# Revit family: ATI - Variable Frequency AC Drive
name_source: partatom
category: Electrical Equipment
revit_build: Autodesk Revit 2014 (Build: 20131024_2115(x64)
units: mm (PartAtom-declared; Revit-internal decimal feet)

## types (4) — shared parameters
Apparent Load A = 0 VA
Apparent Load B = 0 VA
Apparent Load C = 0 VA
Cabinet Material = <By Category>
Circuit Breaker Disconnect Material = <By Category>
Default Elevation = 4' - 0"
Drive Controller Voltage = 460 V
Drive Width = 1' - 1 3/4"
Load Classification = Other
Number of Poles = 3
Pilot Light Material = <By Category>
Pushbotton Material = <By Category>

## per-type parameters (varying)
| type | Drive Height | Drive Length | Front Clearance Depth | Half Drive Length |
| 1-7.5 HP | 3' - 2" | 1' - 7 1/2" | 3' - 0" | 0' - 9 3/4" |
| 10-20 HP | 3' - 2" | 1' - 7 1/2" | 3' - 0" | 0' - 9 3/4" |
| 25-50 HP | 3' - 10" | 1' - 8" | 3' - 6" | 0' - 10" |
| 60-100 HP | 5' - 0" | 2' - 1" | 3' - 6" | 1' - 0 1/2" |

## geometry (parser evidence)
native form markers: Sweep x6
no freeform markers — native parametric forms only
